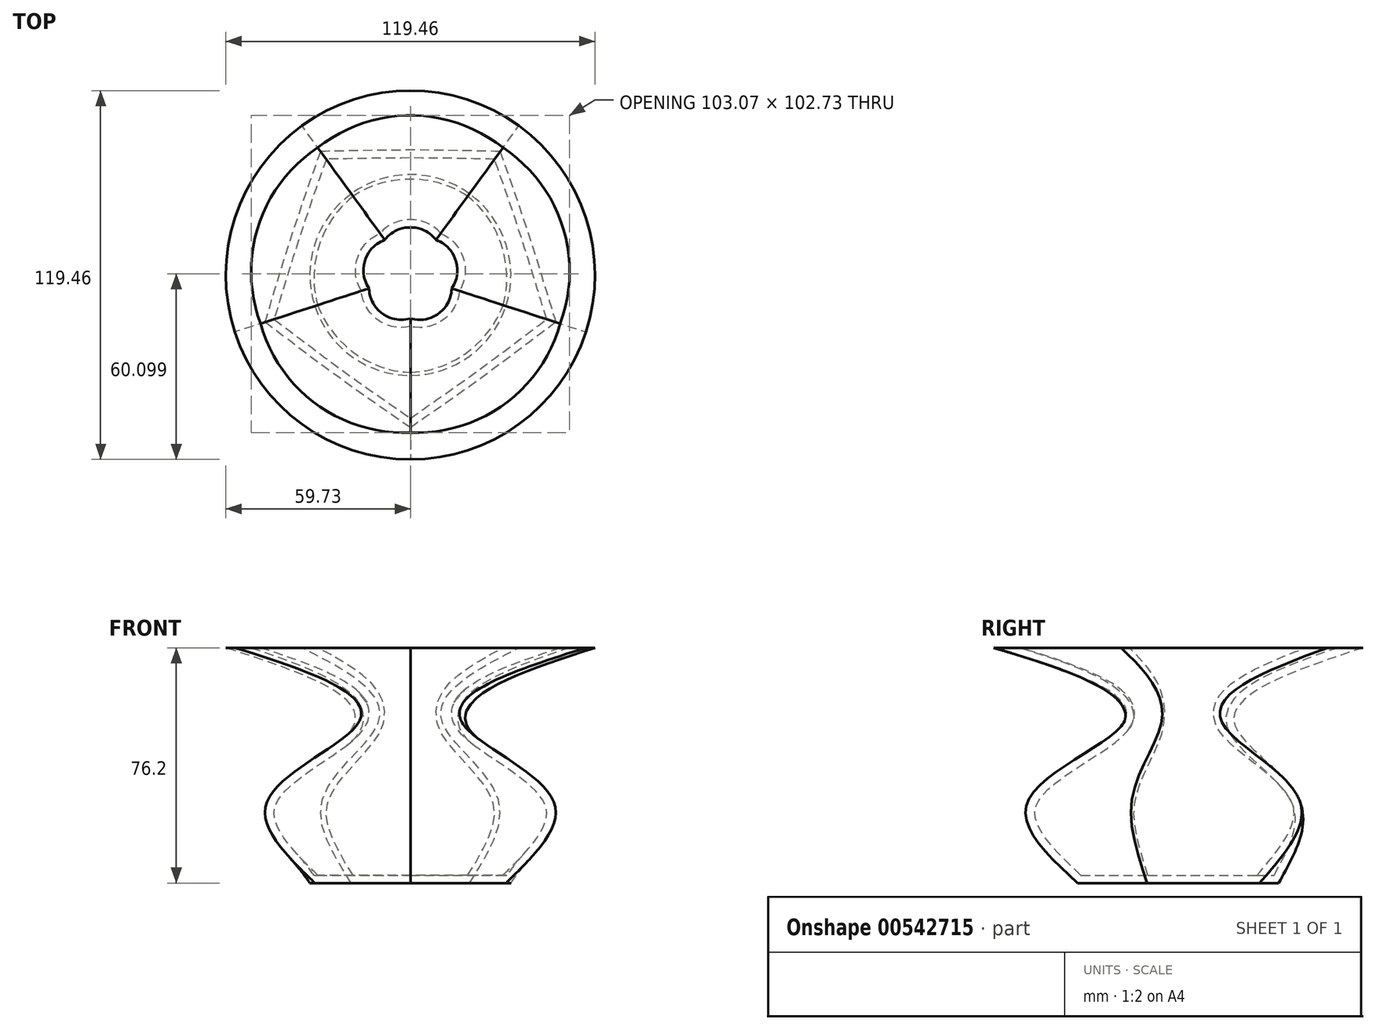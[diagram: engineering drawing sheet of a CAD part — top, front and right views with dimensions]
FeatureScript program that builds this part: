
annotation { "Feature Type Name" : "Feature", "Feature Type Description" : "" }
export const myFeature = defineFeature(function(context is Context, id is Id, definition is map)
    precondition{}
    {
        {
            var Q0;
            Q0=qCreatedBy(makeId("Top.planeOp"),FACE);
            var sketch = newSketch(context, id + "F0", { "sketchPlane" : qUnion([Q0])});
            skCircle(sketch, "E0", {"center": v(0, 0) * mm, "radius": 32.53 * mm});
            skSolve(sketch);
        }
        {
            var Q0;
            Q0=qCreatedBy(makeId("Top.planeOp"),FACE);
            cPlane(context, id + "F1", {"entities" : qUnion([Q0]), "cplaneType" : CPlaneType.OFFSET, "offset" : 25.4 * mm, "width" : 152.4 * mm, "height" : 152.4 * mm});
        }
        {
            var Q0;
            Q0=qCreatedBy(id+"F1.planeOp",FACE);
            var sketch = newSketch(context, id + "F2", { "sketchPlane" : qUnion([Q0])});
            skCircle(sketch, "E1.cCircle", {"center": v(0, 0) * mm, "radius": 39.72 * mm, "construction": true});
            skLineSegment(sketch, "E1.0", {"start": v(-28.86, 39.72) * mm, "end": v(28.86, 39.72) * mm});
            skLineSegment(sketch, "E1.1", {"start": v(28.86, 39.72) * mm, "end": v(46.7, -15.17) * mm});
            skLineSegment(sketch, "E1.2", {"start": v(46.7, -15.17) * mm, "end": v(0, -49.1) * mm});
            skLineSegment(sketch, "E1.3", {"start": v(0, -49.1) * mm, "end": v(-46.7, -15.17) * mm});
            skLineSegment(sketch, "E1.4", {"start": v(-46.7, -15.17) * mm, "end": v(-28.86, 39.72) * mm});
            skPoint(sketch, "E1.0.midPoint", {"position": v(0, 39.72) * mm});
            skSolve(sketch);
        }
        {
            var Q0;
            Q0=qCreatedBy(id+"F1.planeOp",FACE);
            cPlane(context, id + "F3", {"entities" : qUnion([Q0]), "cplaneType" : CPlaneType.OFFSET, "offset" : 25.4 * mm, "width" : 152.4 * mm, "height" : 152.4 * mm});
        }
        {
            var Q0;
            Q0=qCreatedBy(id+"F3.planeOp",FACE);
            var sketch = newSketch(context, id + "F4", { "sketchPlane" : qUnion([Q0])});
            skCircle(sketch, "E2", {"center": v(0, 0) * mm, "radius": 18.42 * mm});
            skSolve(sketch);
        }
        {
            var Q0;
            Q0=qCreatedBy(id+"F3.planeOp",FACE);
            cPlane(context, id + "F5", {"entities" : qUnion([Q0]), "cplaneType" : CPlaneType.OFFSET, "offset" : 25.4 * mm, "width" : 152.4 * mm, "height" : 152.4 * mm});
        }
        {
            var Q0;
            Q0=qCreatedBy(id+"F5.planeOp",FACE);
            var sketch = newSketch(context, id + "F6", { "sketchPlane" : qUnion([Q0])});
            skCircle(sketch, "E3", {"center": v(0, 0) * mm, "radius": 59.73 * mm});
            skSolve(sketch);
        }
        {
            var Q0;
            Q0=makeQuery(id+"F0.imprint","IMPRINT",FACE,{"disambiguationData":[TD([[makeQuery(id+"F0.imprint","IMPRINT",EDGE,{"derivedFrom":sQuery(id+"F0.wireOp",EDGE,"E0")}),1.0]])]});
            var Q1;
            Q1=makeQuery(id+"F2.imprint","IMPRINT",FACE,{"disambiguationData":[TD([[makeQuery(id+"F2.imprint","IMPRINT",EDGE,{"derivedFrom":sQuery(id+"F2.wireOp",EDGE,"E1.0")}),-1.0]])]});
            var Q2;
            Q2=makeQuery(id+"F4.imprint","IMPRINT",FACE,{"disambiguationData":[TD([[makeQuery(id+"F4.imprint","IMPRINT",EDGE,{"derivedFrom":sQuery(id+"F4.wireOp",EDGE,"E2")}),1.0]])]});
            var Q3;
            Q3=makeQuery(id+"F6.imprint","IMPRINT",FACE,{"disambiguationData":[TD([[makeQuery(id+"F6.imprint","IMPRINT",EDGE,{"derivedFrom":sQuery(id+"F6.wireOp",EDGE,"E3")}),1.0]])]});
            loft(context, id + "F7", {"sheetProfilesArray" : [{ "sheetProfileEntities" : qUnion([Q0]) }, { "sheetProfileEntities" : qUnion([Q1]) }, { "sheetProfileEntities" : qUnion([Q2]) }, { "sheetProfileEntities" : qUnion([Q3]) }]});
        }
        {
            var Q0;
            Q0=makeQuery(id+"F7.opLoft","CAP_FACE",FACE,{"disambiguationData":[OSD([makeQuery(id+"F6.imprint","IMPRINT",FACE,{"disambiguationData":[TD([[makeQuery(id+"F6.imprint","IMPRINT",EDGE,{"derivedFrom":sQuery(id+"F6.wireOp",EDGE,"E3")}),1.0]])]})])],"isStart":true});
            shell(context, id + "F8", {"entities" : qUnion([Q0]), "thickness" : 2.54 * mm});
        }
    });
